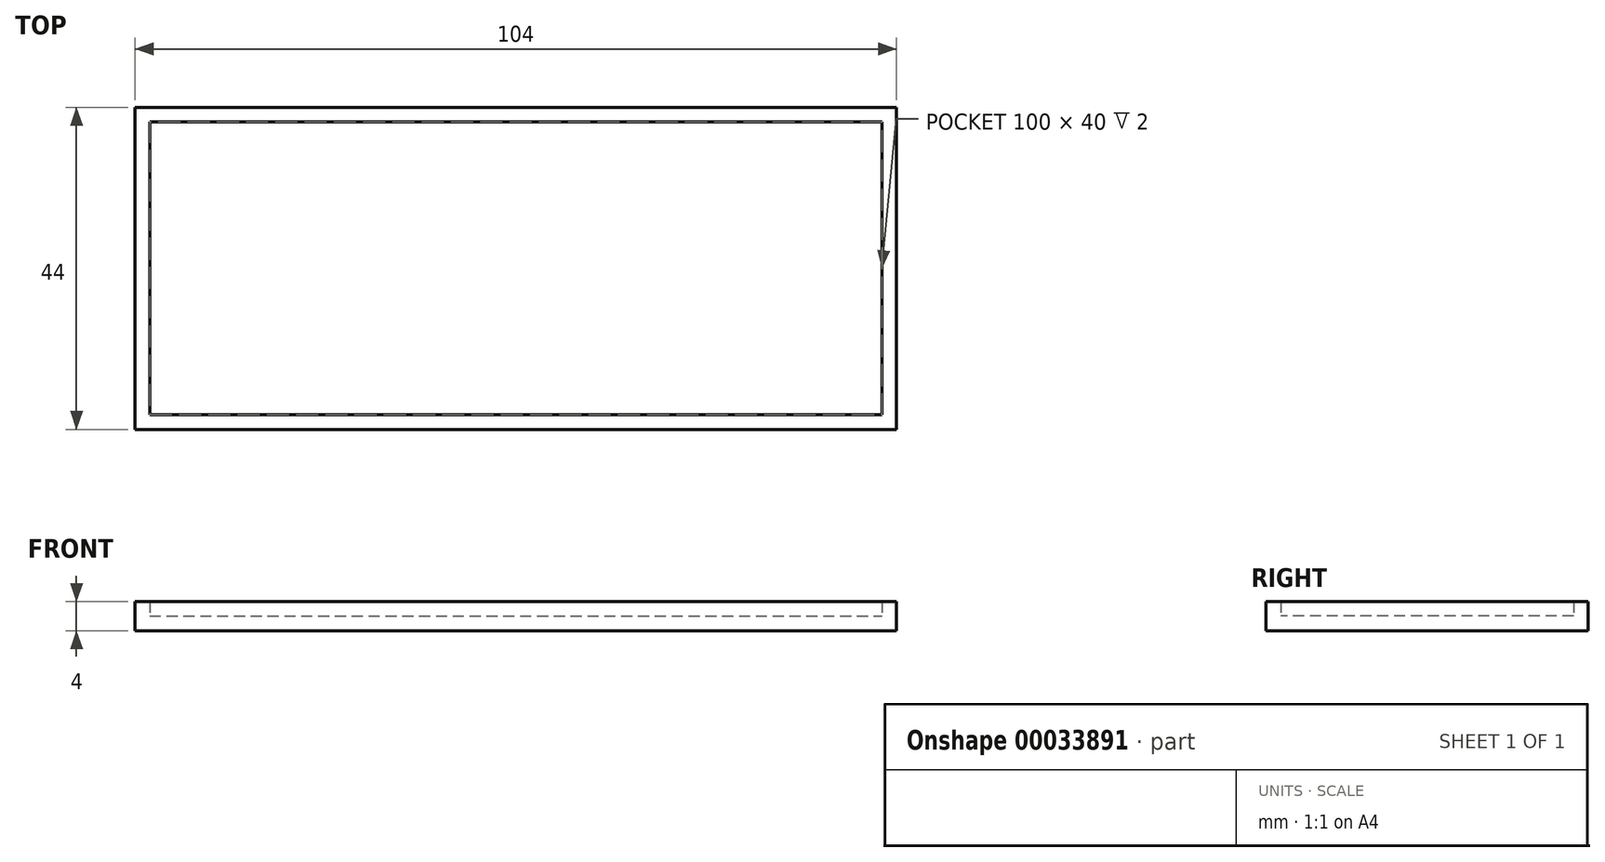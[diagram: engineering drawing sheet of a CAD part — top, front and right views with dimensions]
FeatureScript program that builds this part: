
annotation { "Feature Type Name" : "Feature", "Feature Type Description" : "" }
export const myFeature = defineFeature(function(context is Context, id is Id, definition is map)
    precondition{}
    {
        {
            var Q0;
            Q0=qCreatedBy(makeId("Top.planeOp"),FACE);
            var sketch = newSketch(context, id + "F0", { "sketchPlane" : qUnion([Q0])});
            skLineSegment(sketch, "E0.bottom", {"start": v(-104, 22) * mm, "end": v(0, 22) * mm});
            skLineSegment(sketch, "E0.top", {"start": v(-104, -22) * mm, "end": v(0, -22) * mm});
            skLineSegment(sketch, "E0.left", {"start": v(-104, 22) * mm, "end": v(-104, -22) * mm});
            skLineSegment(sketch, "E0.right", {"start": v(0, 22) * mm, "end": v(0, -22) * mm});
            skSolve(sketch);
        }
        {
            var Q0;
            Q0=makeQuery(id+"F0.imprint","IMPRINT",FACE,{"disambiguationData":[TD([[makeQuery(id+"F0.imprint","IMPRINT",EDGE,{"derivedFrom":sQuery(id+"F0.wireOp",EDGE,"E0.bottom")}),-1.0]])]});
            extrude(context, id + "F1", {"entities" : qUnion([Q0]), "depth" : 4 * mm});
        }
        {
            var Q0;
            Q0=makeQuery(id+"F1.opExtrude","CAP_FACE",FACE,{"disambiguationData":[OSD([sQuery(id+"F0.wireOp",EDGE,"E0.bottom"),sQuery(id+"F0.wireOp",EDGE,"E0.top"),sQuery(id+"F0.wireOp",EDGE,"E0.left"),sQuery(id+"F0.wireOp",EDGE,"E0.right")])],"isStart":false});
            shell(context, id + "F2", {"entities" : qUnion([Q0]), "thickness" : 2 * mm});
        }
        {
            var Q0;
            Q0=makeQuery(id+"F0.imprint","IMPRINT",FACE,{"disambiguationData":[TD([[makeQuery(id+"F0.imprint","IMPRINT",EDGE,{"derivedFrom":sQuery(id+"F0.wireOp",EDGE,"E0.bottom")}),-1.0]])]});
            var sketch = newSketch(context, id + "F3", { "sketchPlane" : qUnion([Q0])});
            skLineSegment(sketch, "E1", {"start": v(-141.78, -20) * mm, "end": v(33.2, -20) * mm, "construction": true});
            skArc(sketch, "E2", {"start": v(-20, -22.12) * mm, "mid": v(-52, -20.77) * mm, "end": v(-84, -22.12) * mm});
            skLineSegment(sketch, "E3.bottom", {"start": v(-84, -36.76) * mm, "end": v(-20, -36.76) * mm});
            skLineSegment(sketch, "E3.left", {"start": v(-84, -36.76) * mm, "end": v(-84, -22.12) * mm});
            skLineSegment(sketch, "E3.right", {"start": v(-20, -36.76) * mm, "end": v(-20, -22.12) * mm});
            skLineSegment(sketch, "E4.MirrorCS", {"start": v(-20, 36.76) * mm, "end": v(-20, 22.12) * mm});
            skLineSegment(sketch, "E5.MirrorCS", {"start": v(-84, 36.76) * mm, "end": v(-20, 36.76) * mm});
            skLineSegment(sketch, "E6.MirrorCS", {"start": v(-84, 36.76) * mm, "end": v(-84, 22.12) * mm});
            skArc(sketch, "E7.MirrorCS", {"start": v(-20, 22.12) * mm, "mid": v(-52, 20.77) * mm, "end": v(-84, 22.12) * mm});
            skSolve(sketch);
        }
        {
            var Q0;
            Q0=makeQuery(id+"F3.imprint","IMPRINT",FACE,{"disambiguationData":[TD([[makeQuery(id+"F3.imprint","IMPRINT",EDGE,{"derivedFrom":sQuery(id+"F3.wireOp",EDGE,"E5.MirrorCS")}),-1.0]])]});
            var Q1;
            Q1=makeQuery(id+"F3.imprint","IMPRINT",FACE,{"disambiguationData":[TD([[makeQuery(id+"F3.imprint","IMPRINT",EDGE,{"derivedFrom":sQuery(id+"F3.wireOp",EDGE,"E3.bottom")}),1.0]])]});
            extrude(context, id + "F4", {"entities" : qUnion([Q0, Q1]), "operationType" : NewBodyOperationType.REMOVE, "depth" : 10 * mm});
        }
    });
